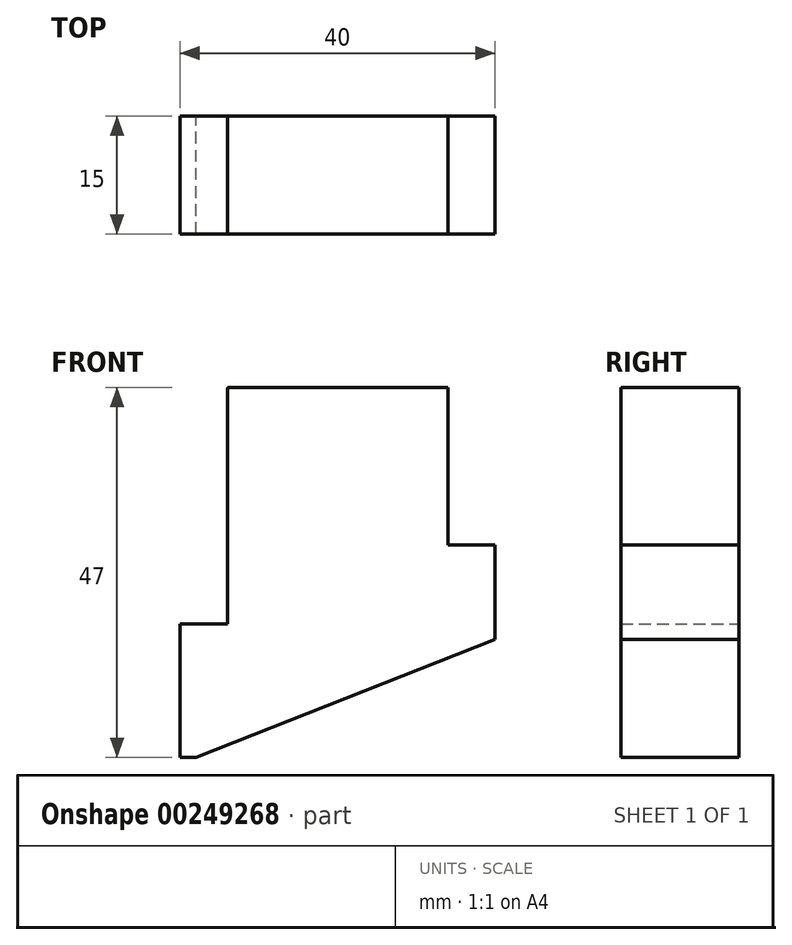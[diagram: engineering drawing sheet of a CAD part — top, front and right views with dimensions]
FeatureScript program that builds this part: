
annotation { "Feature Type Name" : "Feature", "Feature Type Description" : "" }
export const myFeature = defineFeature(function(context is Context, id is Id, definition is map)
    precondition{}
    {
        {
            var Q0;
            Q0=qCreatedBy(makeId("Front.planeOp"),FACE);
            var sketch = newSketch(context, id + "F0", { "sketchPlane" : qUnion([Q0])});
            skLineSegment(sketch, "E0", {"start": v(0, -32) * mm, "end": v(-38, -47) * mm});
            skLineSegment(sketch, "E1", {"start": v(-38, -47) * mm, "end": v(-40, -47) * mm});
            skLineSegment(sketch, "E2", {"start": v(-40, -47) * mm, "end": v(-40, -30) * mm});
            skLineSegment(sketch, "E3", {"start": v(-34, 0) * mm, "end": v(-6, 0) * mm});
            skLineSegment(sketch, "E4", {"start": v(0, -32) * mm, "end": v(0, -20) * mm});
            skLineSegment(sketch, "E5", {"start": v(-40, -30) * mm, "end": v(-34, -30) * mm});
            skLineSegment(sketch, "E6", {"start": v(-34, -30) * mm, "end": v(-34, 0) * mm});
            skLineSegment(sketch, "E7", {"start": v(-6, 0) * mm, "end": v(-6, -20) * mm});
            skLineSegment(sketch, "E8", {"start": v(-6, -20) * mm, "end": v(0, -20) * mm});
            skPoint(sketch, "E9.orphan", {"position": v(0, 0) * mm});
            skSolve(sketch);
        }
        {
            var Q0;
            Q0=makeQuery(id+"F0.imprint","IMPRINT",FACE,{"disambiguationData":[TD([[makeQuery(id+"F0.imprint","IMPRINT",EDGE,{"derivedFrom":sQuery(id+"F0.wireOp",EDGE,"E0")}),-1.0]])]});
            extrude(context, id + "F1", {"entities" : qUnion([Q0]), "depth" : 15 * mm, "symmetric" : true});
        }
    });
